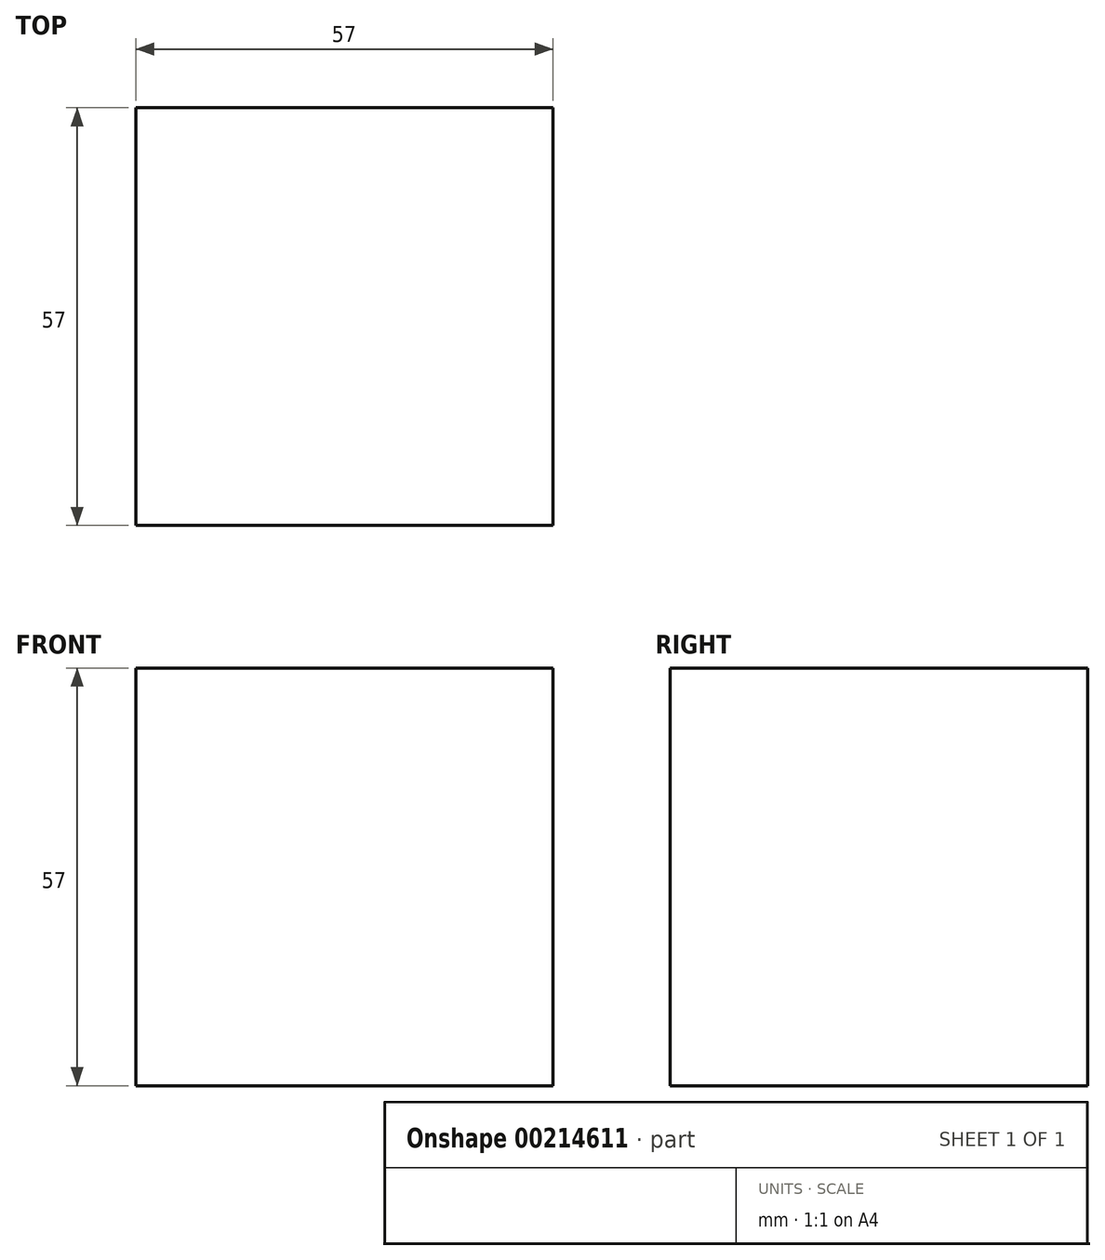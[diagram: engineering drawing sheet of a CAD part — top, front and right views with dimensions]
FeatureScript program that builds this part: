
annotation { "Feature Type Name" : "Feature", "Feature Type Description" : "" }
export const myFeature = defineFeature(function(context is Context, id is Id, definition is map)
    precondition{}
    {
        {
            var Q0;
            Q0=qCreatedBy(makeId("Top.planeOp"),FACE);
            var sketch = newSketch(context, id + "F0", { "sketchPlane" : qUnion([Q0])});
            skLineSegment(sketch, "E0.bottom", {"start": v(-29.07, 22.35) * mm, "end": v(27.93, 22.35) * mm});
            skLineSegment(sketch, "E0.top", {"start": v(-29.07, -34.65) * mm, "end": v(27.93, -34.65) * mm});
            skLineSegment(sketch, "E0.left", {"start": v(-29.07, 22.35) * mm, "end": v(-29.07, -34.65) * mm});
            skLineSegment(sketch, "E0.right", {"start": v(27.93, 22.35) * mm, "end": v(27.93, -34.65) * mm});
            skSolve(sketch);
        }
        {
            var Q0;
            Q0 = qSketchRegion(id + "F0", true);
            extrude(context, id + "F1", {"entities" : qUnion([Q0]), "depth" : 57 * mm});
        }
    });
